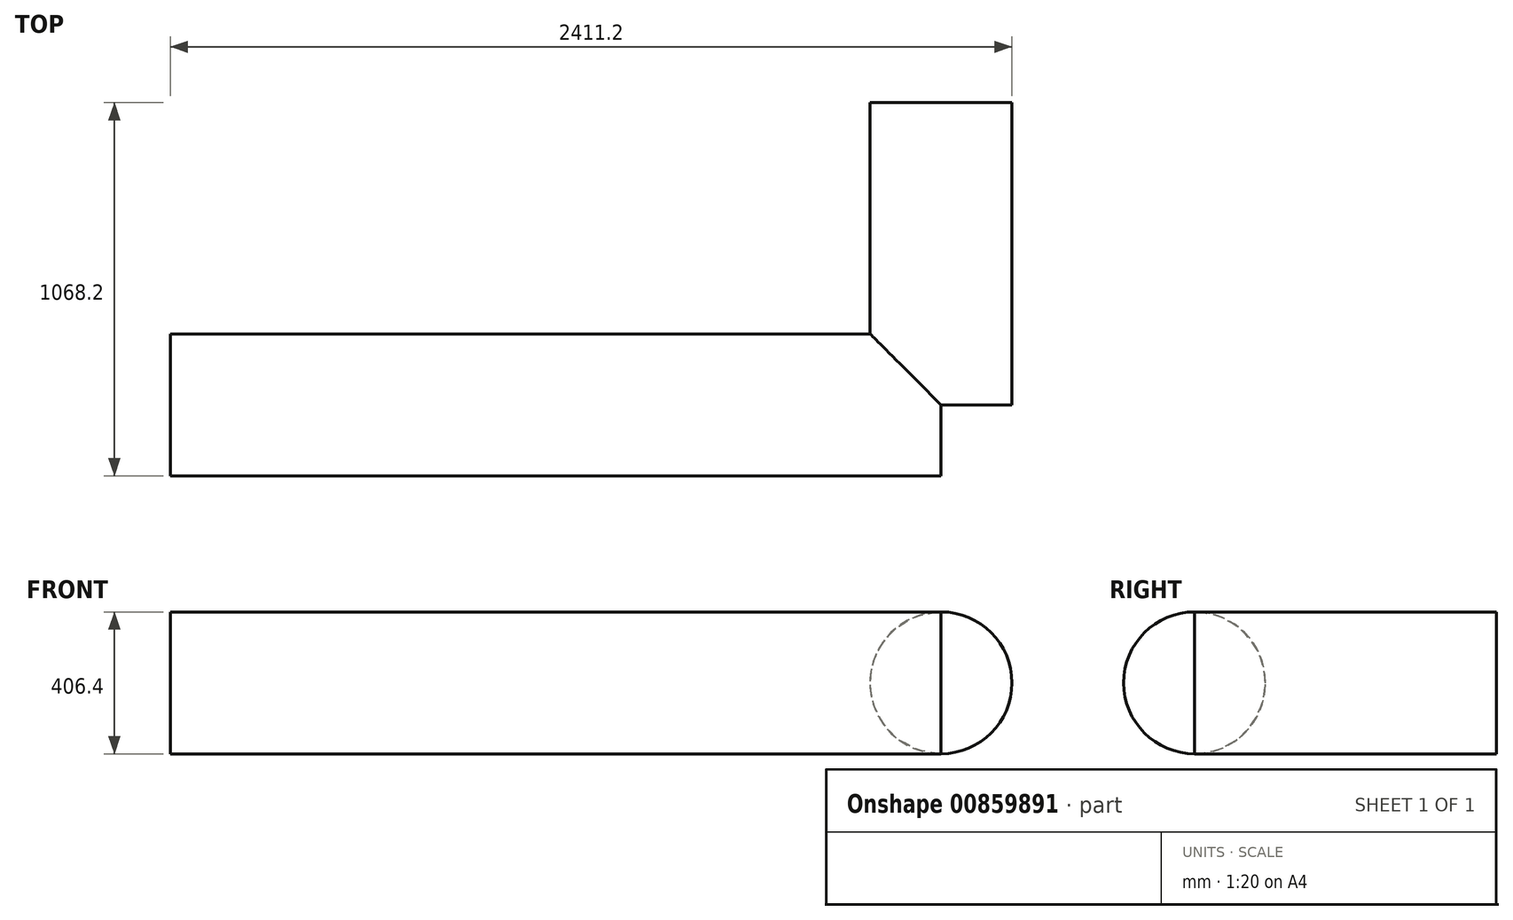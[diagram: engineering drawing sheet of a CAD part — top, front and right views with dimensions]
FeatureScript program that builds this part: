
annotation { "Feature Type Name" : "Feature", "Feature Type Description" : "" }
export const myFeature = defineFeature(function(context is Context, id is Id, definition is map)
    precondition{}
    {
        {
            var Q0;
            Q0=qCreatedBy(makeId("Top.planeOp"),FACE);
            var sketch = newSketch(context, id + "F0", { "sketchPlane" : qUnion([Q0])});
            skLineSegment(sketch, "E0", {"start": v(0, 0) * mm, "end": v(0, -865) * mm});
            skLineSegment(sketch, "E1", {"start": v(0, -865) * mm, "end": v(-2208, -865) * mm});
            skSolve(sketch);
        }
        {
            var Q0;
            Q0=qCreatedBy(makeId("Front.planeOp"),FACE);
            var sketch = newSketch(context, id + "F1", { "sketchPlane" : qUnion([Q0])});
            skCircle(sketch, "E2", {"center": v(0, 0) * mm, "radius": 203.2 * mm});
            skSolve(sketch);
        }
        {
            var Q0;
            Q0 = qSketchRegion(id + "F1", true);
            extrude(context, id + "F2", {"entities" : qUnion([Q0]), "depth" : 865 * mm, "offsetDistance" : 25 * mm});
        }
        {
            var Q0;
            Q0=qCreatedBy(makeId("Right.planeOp"),FACE);
            var sketch = newSketch(context, id + "F3", { "sketchPlane" : qUnion([Q0])});
            skCircle(sketch, "E3", {"center": v(-865, 0) * mm, "radius": 203.2 * mm});
            skSolve(sketch);
        }
        {
            var Q0;
            Q0 = qSketchRegion(id + "F3", true);
            extrude(context, id + "F4", {"entities" : qUnion([Q0]), "operationType" : NewBodyOperationType.ADD, "oppositeDirection" : true, "depth" : 2208 * mm, "offsetDistance" : 25 * mm});
        }
    });
